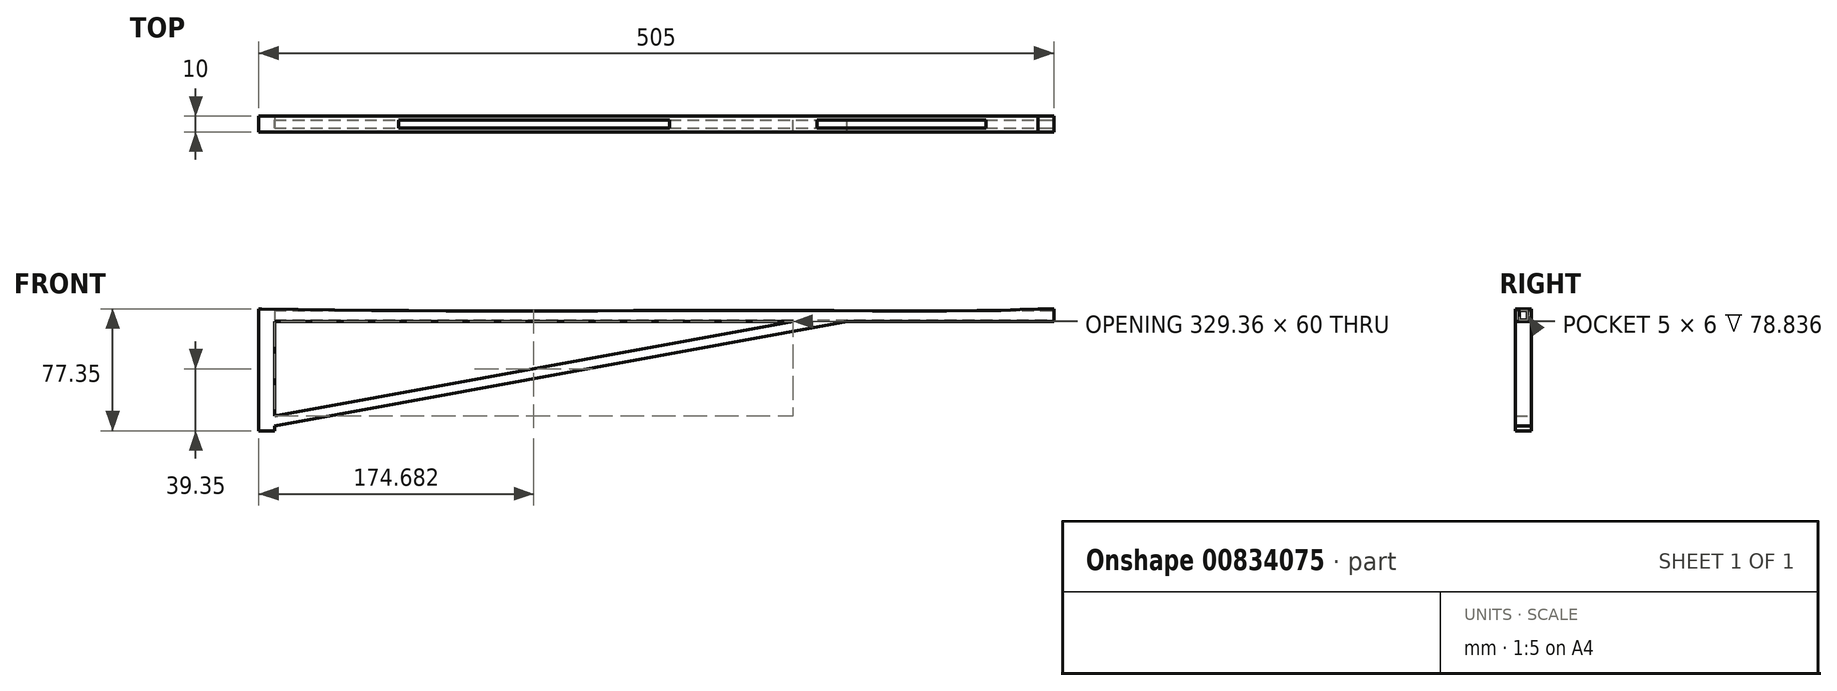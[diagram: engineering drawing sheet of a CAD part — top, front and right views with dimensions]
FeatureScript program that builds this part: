
annotation { "Feature Type Name" : "Feature", "Feature Type Description" : "" }
export const myFeature = defineFeature(function(context is Context, id is Id, definition is map)
    precondition{}
    {
        {
            var Q0;
            Q0=qCreatedBy(makeId("Front.planeOp"),FACE);
            var sketch = newSketch(context, id + "F0", { "sketchPlane" : qUnion([Q0])});
            skLineSegment(sketch, "E0", {"start": v(0, 0) * mm, "end": v(339.36, 0) * mm});
            skLineSegment(sketch, "E1", {"start": v(0, -80) * mm, "end": v(0, 0) * mm});
            skLineSegment(sketch, "E2", {"start": v(10, 0) * mm, "end": v(10, -60) * mm});
            skLineSegment(sketch, "E3", {"start": v(10, -60) * mm, "end": v(339.36, 0) * mm});
            skLineSegment(sketch, "E4", {"start": v(373.72, 0) * mm, "end": v(10, -66.26) * mm});
            skLineSegment(sketch, "E5", {"start": v(10, -66.26) * mm, "end": v(10, -80) * mm});
            skLineSegment(sketch, "E6", {"start": v(10, -80) * mm, "end": v(0, -80) * mm});
            skLineSegment(sketch, "E7.trimOffspring", {"start": v(373.72, 0) * mm, "end": v(505, 0) * mm});
            skLineSegment(sketch, "E8", {"start": v(0, 0) * mm, "end": v(0, 8) * mm});
            skLineSegment(sketch, "E9", {"start": v(505, 8) * mm, "end": v(505, 0) * mm});
            skFitSpline(sketch, "E10", {"points": [v(0, 8) * mm, v(122.9, 6.8) * mm, v(247.3, 6.95) * mm, v(342.78, 7.04) * mm, v(458.58, 6.95) * mm, v(495, 8) * mm], "startDerivative": vector(537.28, -6.93) * mm, "endDerivative": vector(269.65, 9.74) * mm});
            skLineSegment(sketch, "E11.trimOffspring", {"start": v(495, 8) * mm, "end": v(505, 8) * mm});
            skPoint(sketch, "E12", {"position": v(1.88, 7.98) * mm});
            skFitSpline(sketch, "E13", {"points": [v(1.88, 7.98) * mm, v(0.7, 8.31) * mm, v(0, 9.12) * mm], "startDerivative": vector(-2.52, 0.38) * mm, "endDerivative": vector(-1.23, 1.93) * mm});
            skLineSegment(sketch, "E14", {"start": v(0, 8) * mm, "end": v(0, 9.12) * mm});
            skSolve(sketch);
        }
        {
            var Q0;
            Q0=makeQuery(id+"F0.imprint","IMPRINT",FACE,{"disambiguationData":[TD([[makeQuery(id+"F0.imprint","IMPRINT",EDGE,{"derivedFrom":sQuery(id+"F0.wireOp",EDGE,"E1")}),-1.0]])]});
            extrude(context, id + "F1", {"entities" : qUnion([Q0]), "depth" : 10 * mm, "offsetDistance" : 25 * mm});
        }
        {
            var Q0;
            Q0=makeQuery(id+"F1.opExtrude","SWEPT_FACE",FACE,{"disambiguationData":[OSD([sQuery(id+"F0.wireOp",EDGE,"E9")])]});
            var sketch = newSketch(context, id + "F2", { "sketchPlane" : qUnion([Q0])});
            skLineSegment(sketch, "E15", {"start": v(-5, 0) * mm, "end": v(-5, 0) * mm});
            skLineSegment(sketch, "E16", {"start": v(-7.5, 7) * mm, "end": v(-7.5, 1) * mm});
            skLineSegment(sketch, "E17.MirrorCS", {"start": v(-2.5, 7) * mm, "end": v(-2.5, 1) * mm});
            skLineSegment(sketch, "E18", {"start": v(-7.5, 7) * mm, "end": v(-2.5, 7) * mm});
            skLineSegment(sketch, "E19", {"start": v(-7.5, 1) * mm, "end": v(-2.5, 1) * mm});
            skSolve(sketch);
        }
        {
            var Q0;
            {var subQ5=sQuery(id+"F2.wireOp",EDGE,"E16");Q0=makeQuery(id+"F2.imprint","IMPRINT",FACE,{"disambiguationData":[TD([[makeQuery(id+"F2.imprint","IMPRINT",EDGE,{"derivedFrom":subQ5}),1.0]])]});}
            var Q1;
            {var subQ5=sQuery(id+"F2.wireOp",EDGE,"E17.MirrorCS");Q1=makeQuery(id+"F2.imprint","IMPRINT",FACE,{"disambiguationData":[TD([[makeQuery(id+"F2.imprint","IMPRINT",EDGE,{"derivedFrom":subQ5}),-1.0]])]});}
            extrude(context, id + "F3", {"entities" : qUnion([Q0, Q1]), "operationType" : NewBodyOperationType.REMOVE, "oppositeDirection" : true, "depth" : 495 * mm, "offsetDistance" : 25 * mm});
        }
        {
            var Q0;
            Q0=makeQuery(id+"F1.opExtrude","CAP_FACE",FACE,{"disambiguationData":[OSD([sQuery(id+"F0.wireOp",EDGE,"E0"),sQuery(id+"F0.wireOp",EDGE,"E1"),sQuery(id+"F0.wireOp",EDGE,"E2"),sQuery(id+"F0.wireOp",EDGE,"E3"),sQuery(id+"F0.wireOp",EDGE,"E4"),sQuery(id+"F0.wireOp",EDGE,"E5"),sQuery(id+"F0.wireOp",EDGE,"E6"),sQuery(id+"F0.wireOp",EDGE,"E7.trimOffspring"),sQuery(id+"F0.wireOp",EDGE,"E8"),sQuery(id+"F0.wireOp",EDGE,"E9"),sQuery(id+"F0.wireOp",EDGE,"E10"),sQuery(id+"F0.wireOp",EDGE,"E11.trimOffspring"),sQuery(id+"F0.wireOp",EDGE,"E13"),sQuery(id+"F0.wireOp",EDGE,"E14")])],"isStart":false});
            var sketch = newSketch(context, id + "F4", { "sketchPlane" : qUnion([Q0])});
            skLineSegment(sketch, "E20", {"start": v(10, -69.35) * mm, "end": v(0, -69.35) * mm});
            skLineSegment(sketch, "E21", {"start": v(0, -69.35) * mm, "end": v(0, -80) * mm});
            skLineSegment(sketch, "E22", {"start": v(0, -80) * mm, "end": v(10, -80) * mm});
            skLineSegment(sketch, "E23", {"start": v(10, -80) * mm, "end": v(10, -69.35) * mm});
            skSolve(sketch);
        }
        {
            var Q0;
            Q0=makeQuery(id+"F4.imprint","IMPRINT",FACE,{"disambiguationData":[TD([[makeQuery(id+"F4.imprint","IMPRINT",EDGE,{"derivedFrom":sQuery(id+"F4.wireOp",EDGE,"E20")}),1.0]])]});
            extrude(context, id + "F5", {"entities" : qUnion([Q0]), "operationType" : NewBodyOperationType.REMOVE, "oppositeDirection" : true, "depth" : 25 * mm, "offsetDistance" : 25 * mm});
        }
    });
